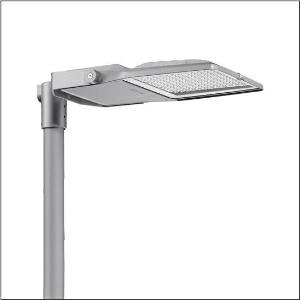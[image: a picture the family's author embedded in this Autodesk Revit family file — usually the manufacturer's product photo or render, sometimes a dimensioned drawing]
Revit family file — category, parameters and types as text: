
# Revit family: floodlight_fl_21_iq_midi___pl64_5xa7781e2e3a_93f0
name_source: partatom
category: Lighting Fixtures
units: mm (PartAtom-declared; Revit-internal decimal feet)

## family parameters
Cut with Voids When Loaded = No
Host = Face
Light Source = No
Part Type = Normal
Room Calculation Point = No
Round Connector Dimension = Use Diameter
Shared = No

## types (1)
- --- (1 x LED, 25930 lm, 208.1 W, 3000K)
    Apparent Load = 208 VA
    CIE Flux Codes = 28 80 98 100 100
    Color Rendering = 70
    Color Temperature = 3000K
    Default Elevation = 1800 mm
    Description = Floodlight FL 21 iQ midi, floodlight, primary light control with lens, of PMMA, primary optical cover: protective disc, of toughened safety glass, transparent, light distribution: PL64, light emission: direct distribution, installation type: surface-mounted, LED, High Power LED, rated luminous flux: 25.930lm, luminous efficacy: 125lm/W, light colour: 730, colour temperature: 3000K, control gear: ECG iQ, control: optimised constant luminous flux control (CLO 2.0), Desk-Remote (wireless, voltage-free reading and setting of iQ features in the workshop via application-optimized NFC function/RFID function), Light-Fading, Smart-Wire, Night-Set, Lumen-Switch, Temp-Guard, Auto-Match, with terminal, 6-pole, mains connection: 220..240V, AC, 50/60Hz, start of lifetime: 208W, end of service life: 227W, reduction: 90W, luminaire housing, of diecast aluminium, powder-coated, Siteco® metallic grey (DB 702S), corrosivity category C5 mid according to DIN EN ISO 12944, sealing non-destructively replaceable, please order mast flange separately, mast bracket, of steel, galvanised, powder-coated, Siteco® metallic grey (DB 702S), protection rating (complete): IP66, insulation class (complete): insulation class II (safety insulation), certification: CE, protection symbol: D, impact resistance: IK08, permissible operating ambient temperature: -40..+40°C, permissible operating ambient temperature for outdoor applications: -40..+50°C, standard: DIN EN 12944, LABS conformity tested according to VDMA 24364:2018-05, packaging unit: 1 piece

Light Distribution: PL64
    Height = 76 mm
    Lamp = 1 x LED
    Lamp Light Flux = 25930 lm
    Lamp Power = 208.1 W
    Lamp count = 1
    Length = 657 mm
    Luminous efficacy = 125 lm/W
    Manufacturer = Siteco
    ModVariant = No
    Model = 5XA7781E2E3A
    Number of Poles = 1
    OnlyDefault = Yes
    Power Factor = 1
    Product Name = Floodlight FL 21 iQ midi | PL64
    Product group = floodlight | pylon annexe
    ProductGroupID = 6200
    Protection Class = Protection class II
    Protection Degree = IP 66
    RLX_Detail_Level = 1
    RLX_Emergency_Light_Flux = 0 lm
    RLX_Emergency_Type = 0
    RLX_Emergency_Type_DB = No
    RlxData = <blob elided: 153557 chars, md5=f51d9413>
    Socket = socket
    Standby Power = 0 W
    System Light Flux = 25930 lm
    System Power = 208 W
    Type Comments = factory setting: luminous flux: 100 % | dim-lin: 254 | 710 mA
    Type Image = l_1007123.jpg
    URL = http://relux.com
    VarID = @adj_055571
    Voltage = 0 V
    Weight = 0.00 kg
    Width = 442 mm

## geometry (parser evidence)
native form markers: Blend x4, Sweep x11
no freeform markers — native parametric forms only
